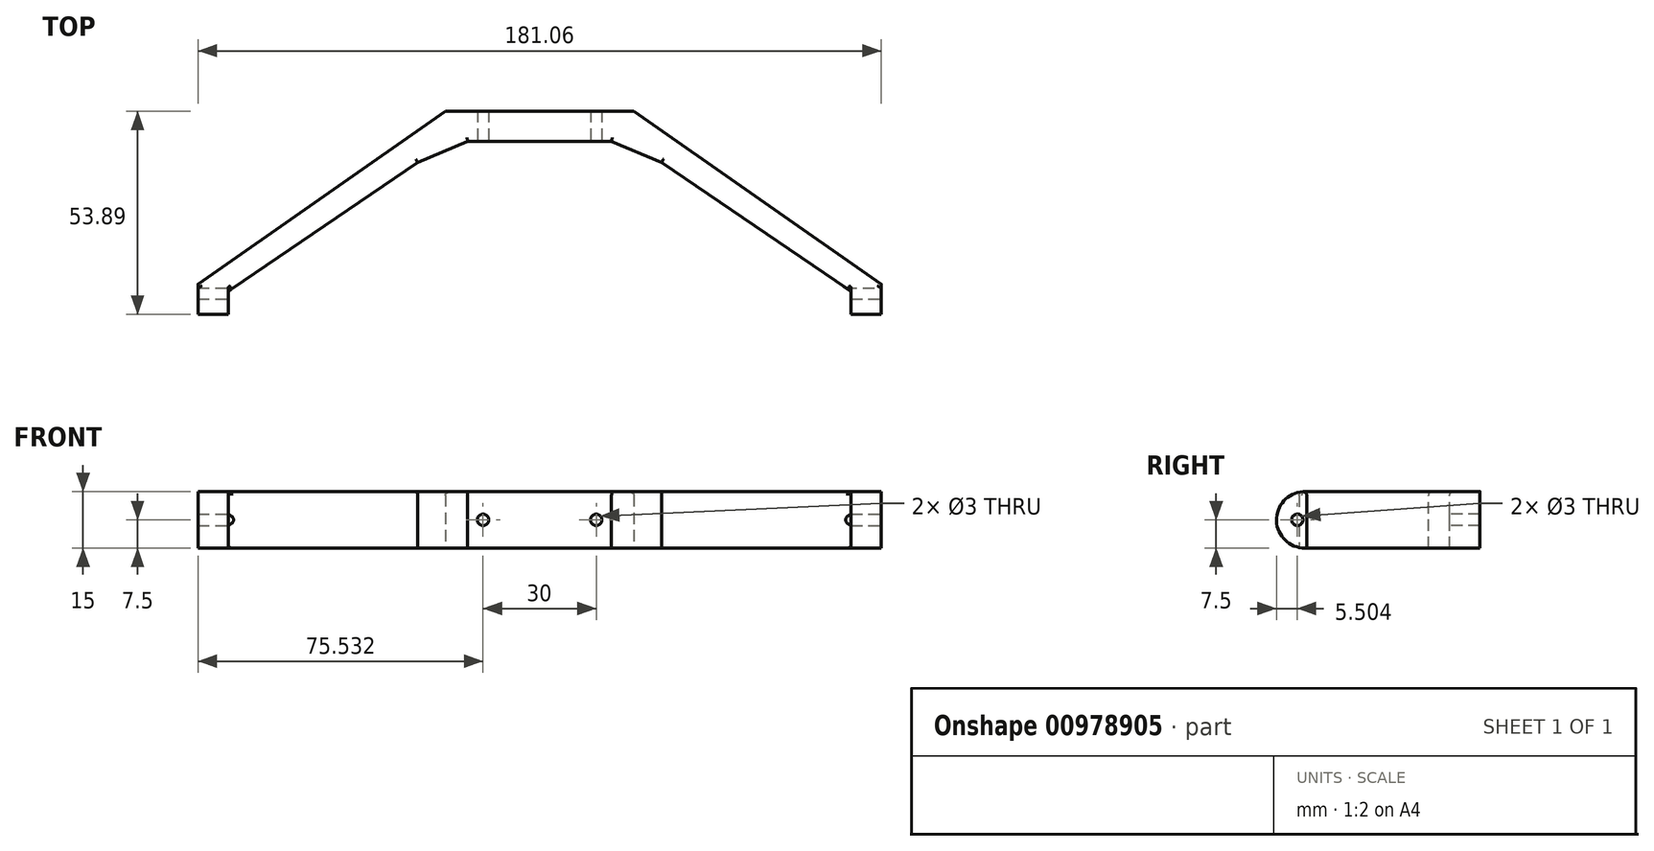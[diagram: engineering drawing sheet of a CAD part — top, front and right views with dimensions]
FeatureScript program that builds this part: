
annotation { "Feature Type Name" : "Feature", "Feature Type Description" : "" }
export const myFeature = defineFeature(function(context is Context, id is Id, definition is map)
    precondition{}
    {
        {
            var Q0;
            Q0=qCreatedBy(makeId("Top.planeOp"),FACE);
            var sketch = newSketch(context, id + "F0", { "sketchPlane" : qUnion([Q0])});
            skLineSegment(sketch, "E0", {"start": v(-29.54, 0) * mm, "end": v(20.46, 0) * mm});
            skLineSegment(sketch, "E1", {"start": v(20.46, 0) * mm, "end": v(86, -45.89) * mm});
            skLineSegment(sketch, "E2", {"start": v(-29.54, 0) * mm, "end": v(-95.07, -45.89) * mm});
            skLineSegment(sketch, "E3.1", {"start": v(-28.6, -8) * mm, "end": v(19.52, -8) * mm});
            skLineSegment(sketch, "E4", {"start": v(-95.07, -45.89) * mm, "end": v(-95.07, -53.89) * mm});
            skLineSegment(sketch, "E5", {"start": v(-95.07, -53.89) * mm, "end": v(-87.07, -53.89) * mm});
            skLineSegment(sketch, "E6", {"start": v(86, -45.89) * mm, "end": v(86, -53.89) * mm});
            skLineSegment(sketch, "E7", {"start": v(86, -53.89) * mm, "end": v(78, -53.89) * mm});
            skLineSegment(sketch, "E8", {"start": v(78, -53.89) * mm, "end": v(78, -47.89) * mm});
            skLineSegment(sketch, "E9", {"start": v(-87.07, -47.89) * mm, "end": v(-28.6, -8) * mm});
            skLineSegment(sketch, "E10", {"start": v(-95.07, -49.89) * mm, "end": v(86, -49.89) * mm, "construction": true});
            skLineSegment(sketch, "E11", {"start": v(19.52, -8) * mm, "end": v(78, -47.89) * mm});
            skLineSegment(sketch, "E12", {"start": v(-87.07, -47.89) * mm, "end": v(-87.07, -53.89) * mm});
            skSolve(sketch);
        }
        {
            var Q0;
            Q0 = qSketchRegion(id + "F0", true);
            extrude(context, id + "F1", {"entities" : qUnion([Q0]), "depth" : 15 * mm, "offsetDistance" : 25 * mm});
        }
        {
            var Q0;
            Q0=makeQuery(id+"F1.opExtrude","SWEPT_FACE",FACE,{"disambiguationData":[OSD([sQuery(id+"F0.wireOp",EDGE,"E3.1")])]});
            var sketch = newSketch(context, id + "F2", { "sketchPlane" : qUnion([Q0])});
            skPoint(sketch, "E13", {"position": v(10.46, 7.5) * mm});
            skPoint(sketch, "E14", {"position": v(-19.54, 7.5) * mm});
            skSolve(sketch);
        }
        {
            var Q0;
            Q0=sQuery(id+"F2.wireOp",VERTEX,"E13");
            var Q1;
            Q1=sQuery(id+"F2.wireOp",VERTEX,"E14");
            var Q2;
            Q2=makeQuery(id+"F1.opExtrude","SWEPT_BODY",BODY,{"disambiguationData":[OSD([sQuery(id+"F0.wireOp",EDGE,"E0"),sQuery(id+"F0.wireOp",EDGE,"E1"),sQuery(id+"F0.wireOp",EDGE,"E2"),sQuery(id+"F0.wireOp",EDGE,"E3.0"),sQuery(id+"F0.wireOp",EDGE,"E3.1"),sQuery(id+"F0.wireOp",EDGE,"E3.2"),sQuery(id+"F0.wireOp",EDGE,"E4"),sQuery(id+"F0.wireOp",EDGE,"E5"),sQuery(id+"F0.wireOp",EDGE,"OdtLC3XA-XJ0s-QaNe-0YCL-I7tE788CnXUg"),sQuery(id+"F0.wireOp",EDGE,"E6"),sQuery(id+"F0.wireOp",EDGE,"E7"),sQuery(id+"F0.wireOp",EDGE,"E8"),sQuery(id+"F0.wireOp",EDGE,"8QT8s7BS-7Lwl-x97F-qdi4-yxx5pLWod5KK"),sQuery(id+"F0.wireOp",EDGE,"bjtlVlTT-dK6R-KiIL-WSG1-F9lOa2L4V2K6")])]});
            hole(context, id + "F3", {"style" : HoleStyle.SIMPLE, "endStyle" : HoleEndStyle.THROUGH, "holeDiameter" : 3 * mm, "majorDiameter" : 5 * mm, "isTappedThrough" : true, "tappedDepth" : 12 * mm, "tapClearance" : 3, "locations" : qUnion([Q0, Q1]), "scope" : qUnion([Q2])});
        }
        {
            var Q0;
            Q0=makeQuery(id+"F1.opExtrude","SWEPT_FACE",FACE,{"disambiguationData":[OSD([sQuery(id+"F0.wireOp",EDGE,"E6")])]});
            var sketch = newSketch(context, id + "F4", { "sketchPlane" : qUnion([Q0])});
            skPoint(sketch, "E15", {"position": v(-48.39, 7.5) * mm});
            skSolve(sketch);
        }
        {
            var Q0;
            Q0=sQuery(id+"F4.wireOp",VERTEX,"E15");
            var Q1;
            Q1=makeQuery(id+"F1.opExtrude","SWEPT_BODY",BODY,{"disambiguationData":[OSD([sQuery(id+"F0.wireOp",EDGE,"E0"),sQuery(id+"F0.wireOp",EDGE,"E1"),sQuery(id+"F0.wireOp",EDGE,"E2"),sQuery(id+"F0.wireOp",EDGE,"E3.0"),sQuery(id+"F0.wireOp",EDGE,"E3.1"),sQuery(id+"F0.wireOp",EDGE,"E3.2"),sQuery(id+"F0.wireOp",EDGE,"E4"),sQuery(id+"F0.wireOp",EDGE,"E5"),sQuery(id+"F0.wireOp",EDGE,"OdtLC3XA-XJ0s-QaNe-0YCL-I7tE788CnXUg"),sQuery(id+"F0.wireOp",EDGE,"E6"),sQuery(id+"F0.wireOp",EDGE,"E7"),sQuery(id+"F0.wireOp",EDGE,"E8"),sQuery(id+"F0.wireOp",EDGE,"8QT8s7BS-7Lwl-x97F-qdi4-yxx5pLWod5KK"),sQuery(id+"F0.wireOp",EDGE,"bjtlVlTT-dK6R-KiIL-WSG1-F9lOa2L4V2K6")])]});
            hole(context, id + "F5", {"style" : HoleStyle.SIMPLE, "endStyle" : HoleEndStyle.THROUGH, "holeDiameter" : 3 * mm, "majorDiameter" : 5 * mm, "isTappedThrough" : true, "tappedDepth" : 12 * mm, "tapClearance" : 3, "locations" : qUnion([Q0]), "scope" : qUnion([Q1])});
        }
        {
            var Q0;
            Q0=makeQuery(id+"F1.opExtrude","CAP_EDGE",EDGE,{"disambiguationData":[OSD([sQuery(id+"F0.wireOp",EDGE,"E7")])],"isStart":true});
            var Q1;
            Q1=makeQuery(id+"F1.opExtrude","CAP_EDGE",EDGE,{"disambiguationData":[OSD([sQuery(id+"F0.wireOp",EDGE,"E7")])],"isStart":false});
            var Q2;
            Q2=makeQuery(id+"F1.opExtrude","CAP_EDGE",EDGE,{"disambiguationData":[OSD([sQuery(id+"F0.wireOp",EDGE,"E5")])],"isStart":true});
            var Q3;
            Q3=makeQuery(id+"F1.opExtrude","CAP_EDGE",EDGE,{"disambiguationData":[OSD([sQuery(id+"F0.wireOp",EDGE,"E5")])],"isStart":false});
            fillet(context, id + "F6", {"entities" : qUnion([Q0, Q1, Q2, Q3]), "radius" : 7.5 * mm, "tangentPropagation" : true, "allowEdgeOverflow" : false});
        }
        {
            var Q0;
            Q0=makeQuery(id+"F1.opExtrude","CAP_EDGE",EDGE,{"disambiguationData":[OSD([sQuery(id+"F0.wireOp",EDGE,"E2")])],"isStart":false});
            var Q1;
            Q1=makeQuery(id+"F1.opExtrude","CAP_EDGE",EDGE,{"disambiguationData":[OSD([sQuery(id+"F0.wireOp",EDGE,"E3.0")])],"isStart":false});
            var Q2;
            Q2=makeQuery(id+"F1.opExtrude","CAP_EDGE",EDGE,{"disambiguationData":[OSD([sQuery(id+"F0.wireOp",EDGE,"E1")])],"isStart":false});
            var Q3;
            Q3=makeQuery(id+"F1.opExtrude","CAP_EDGE",EDGE,{"disambiguationData":[OSD([sQuery(id+"F0.wireOp",EDGE,"E3.2")])],"isStart":false});
            var Q4;
            Q4=makeQuery(id+"F1.opExtrude","CAP_EDGE",EDGE,{"disambiguationData":[OSD([sQuery(id+"F0.wireOp",EDGE,"E3.2")])],"isStart":true});
            fillet(context, id + "F7", {"entities" : qUnion([Q0, Q1, Q2, Q3, Q4]), "radius" : 1 * mm, "tangentPropagation" : true, "allowEdgeOverflow" : false});
        }
        {
            var Q0;
            Q0=makeQuery(id+"F1.opExtrude","SWEPT_EDGE",EDGE,{"disambiguationData":[OSD([sQuery(id+"F0.wireOp",EDGE,"E3.1"),sQuery(id+"F0.wireOp",EDGE,"E9")])]});
            var Q1;
            Q1=makeQuery(id+"F1.opExtrude","SWEPT_EDGE",EDGE,{"disambiguationData":[OSD([sQuery(id+"F0.wireOp",EDGE,"E3.1"),sQuery(id+"F0.wireOp",EDGE,"E11")])]});
            chamfer(context, id + "F8", {"entities" : qUnion([Q0, Q1]), "chamferType" : ChamferType.TWO_OFFSETS, "width1" : 5 * mm, "oppositeDirection" : false, "width2" : 10 * mm, "tangentPropagation" : true});
        }
        {
            var Q0;
            Q0=makeQuery(id+"F1.opExtrude","CAP_EDGE",EDGE,{"disambiguationData":[OSD([sQuery(id+"F0.wireOp",EDGE,"E9")])],"isStart":false});
            var Q1;
            {var subQ0=sQuery(id+"F0.wireOp",EDGE,"E9");var subQ1=sQuery(id+"F0.wireOp",EDGE,"E3.1");Q1=makeQuery(id+"F8.opChamfer","BLEND_EDGE",EDGE,{"blendedFrom":[makeQuery(id+"F1.opExtrude","SWEPT_EDGE",EDGE,{"disambiguationData":[OSD([subQ1,subQ0])]}),makeQuery(id+"F1.opExtrude","CAP_FACE",FACE,{"disambiguationData":[OSD([sQuery(id+"F0.wireOp",EDGE,"E0"),sQuery(id+"F0.wireOp",EDGE,"E1"),sQuery(id+"F0.wireOp",EDGE,"E2"),subQ1,sQuery(id+"F0.wireOp",EDGE,"E4"),sQuery(id+"F0.wireOp",EDGE,"E5"),sQuery(id+"F0.wireOp",EDGE,"OdtLC3XA-XJ0s-QaNe-0YCL-I7tE788CnXUg"),sQuery(id+"F0.wireOp",EDGE,"E6"),sQuery(id+"F0.wireOp",EDGE,"E7"),sQuery(id+"F0.wireOp",EDGE,"E8"),sQuery(id+"F0.wireOp",EDGE,"8QT8s7BS-7Lwl-x97F-qdi4-yxx5pLWod5KK"),subQ0,sQuery(id+"F0.wireOp",EDGE,"E11")])],"isStart":false})],"blendedInto":[makeQuery(id+"F1.opExtrude","CAP_FACE",FACE,{"disambiguationData":[OSD([sQuery(id+"F0.wireOp",EDGE,"E0"),sQuery(id+"F0.wireOp",EDGE,"E1"),sQuery(id+"F0.wireOp",EDGE,"E2"),subQ1,sQuery(id+"F0.wireOp",EDGE,"E4"),sQuery(id+"F0.wireOp",EDGE,"E5"),sQuery(id+"F0.wireOp",EDGE,"OdtLC3XA-XJ0s-QaNe-0YCL-I7tE788CnXUg"),sQuery(id+"F0.wireOp",EDGE,"E6"),sQuery(id+"F0.wireOp",EDGE,"E7"),sQuery(id+"F0.wireOp",EDGE,"E8"),sQuery(id+"F0.wireOp",EDGE,"8QT8s7BS-7Lwl-x97F-qdi4-yxx5pLWod5KK"),subQ0,sQuery(id+"F0.wireOp",EDGE,"E11")])],"isStart":false})]});}
            var Q2;
            Q2=makeQuery(id+"F1.opExtrude","CAP_EDGE",EDGE,{"disambiguationData":[OSD([sQuery(id+"F0.wireOp",EDGE,"E3.1")])],"isStart":false});
            var Q3;
            {var subQ0=sQuery(id+"F0.wireOp",EDGE,"E11");var subQ1=sQuery(id+"F0.wireOp",EDGE,"E3.1");Q3=makeQuery(id+"F8.opChamfer","BLEND_EDGE",EDGE,{"blendedFrom":[makeQuery(id+"F1.opExtrude","SWEPT_EDGE",EDGE,{"disambiguationData":[OSD([subQ1,subQ0])]}),makeQuery(id+"F1.opExtrude","CAP_FACE",FACE,{"disambiguationData":[OSD([sQuery(id+"F0.wireOp",EDGE,"E0"),sQuery(id+"F0.wireOp",EDGE,"E1"),sQuery(id+"F0.wireOp",EDGE,"E2"),subQ1,sQuery(id+"F0.wireOp",EDGE,"E4"),sQuery(id+"F0.wireOp",EDGE,"E5"),sQuery(id+"F0.wireOp",EDGE,"OdtLC3XA-XJ0s-QaNe-0YCL-I7tE788CnXUg"),sQuery(id+"F0.wireOp",EDGE,"E6"),sQuery(id+"F0.wireOp",EDGE,"E7"),sQuery(id+"F0.wireOp",EDGE,"E8"),sQuery(id+"F0.wireOp",EDGE,"8QT8s7BS-7Lwl-x97F-qdi4-yxx5pLWod5KK"),sQuery(id+"F0.wireOp",EDGE,"E9"),subQ0])],"isStart":false})],"blendedInto":[makeQuery(id+"F1.opExtrude","CAP_FACE",FACE,{"disambiguationData":[OSD([sQuery(id+"F0.wireOp",EDGE,"E0"),sQuery(id+"F0.wireOp",EDGE,"E1"),sQuery(id+"F0.wireOp",EDGE,"E2"),subQ1,sQuery(id+"F0.wireOp",EDGE,"E4"),sQuery(id+"F0.wireOp",EDGE,"E5"),sQuery(id+"F0.wireOp",EDGE,"OdtLC3XA-XJ0s-QaNe-0YCL-I7tE788CnXUg"),sQuery(id+"F0.wireOp",EDGE,"E6"),sQuery(id+"F0.wireOp",EDGE,"E7"),sQuery(id+"F0.wireOp",EDGE,"E8"),sQuery(id+"F0.wireOp",EDGE,"8QT8s7BS-7Lwl-x97F-qdi4-yxx5pLWod5KK"),sQuery(id+"F0.wireOp",EDGE,"E9"),subQ0])],"isStart":false})]});}
            var Q4;
            Q4=makeQuery(id+"F1.opExtrude","CAP_EDGE",EDGE,{"disambiguationData":[OSD([sQuery(id+"F0.wireOp",EDGE,"E11")])],"isStart":false});
            fillet(context, id + "F9", {"entities" : qUnion([Q0, Q1, Q2, Q3, Q4]), "radius" : 1 * mm, "tangentPropagation" : true, "allowEdgeOverflow" : false});
        }
    });
